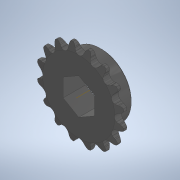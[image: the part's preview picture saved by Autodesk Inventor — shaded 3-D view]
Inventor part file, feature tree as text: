
AUTODESK INVENTOR PART (.ipt)
format: ipt  version: 2020 (Build 240168000, 168)  size: 474,624 bytes
history: native  units: in
note: dims shown in document units (in); Inventor stores cm internally (conversion verified against a paired STEP export)
features: chamfer x1
ambient origin geometry x8: Origin, YZ Plane, XZ Plane, XY Plane, X Axis, Y Axis, Z Axis, Center Point
bodies: Solid1 (feature_tree)
feature tree (1):
  chamfer  "Chamfer2"  [1 undecoded]
note: 1 required parameter value undecoded (feature->parameter linkage not recoverable at this tier; creation-order binding heuristic only, values carry confidence <= 0.55)
